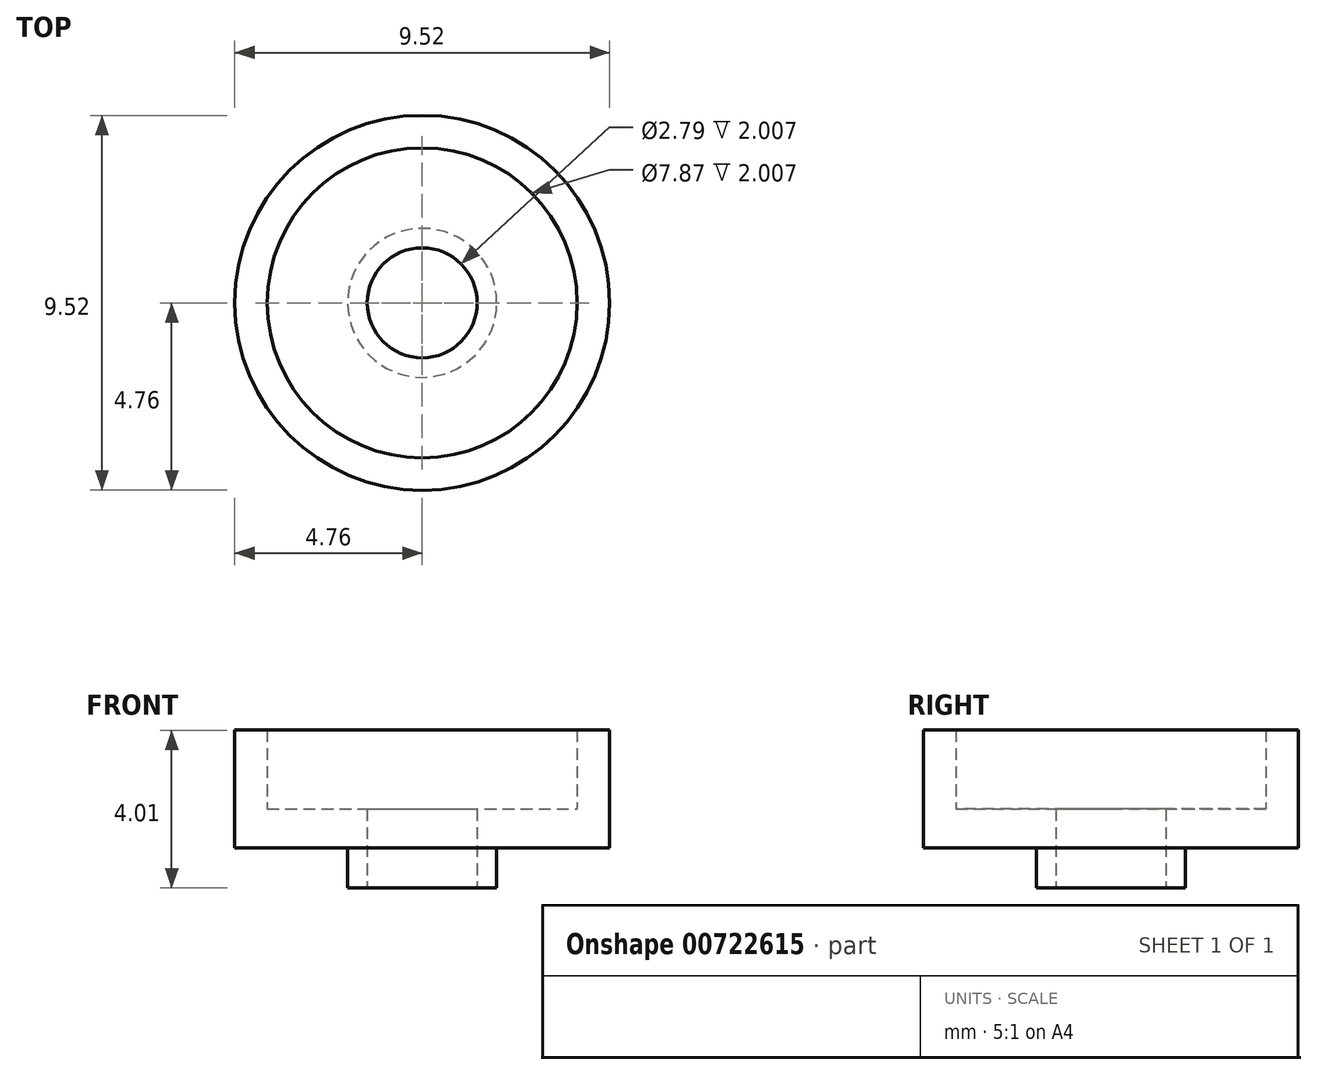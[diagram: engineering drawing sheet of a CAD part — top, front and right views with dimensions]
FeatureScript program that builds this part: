
annotation { "Feature Type Name" : "Feature", "Feature Type Description" : "" }
export const myFeature = defineFeature(function(context is Context, id is Id, definition is map)
    precondition{}
    {
        {
            var Q0;
            Q0=qCreatedBy(makeId("Front.planeOp"),FACE);
            var sketch = newSketch(context, id + "F0", { "sketchPlane" : qUnion([Q0])});
            skLineSegment(sketch, "E0", {"start": v(0, 0) * mm, "end": v(-1.9, 0) * mm});
            skLineSegment(sketch, "E1", {"start": v(-1.9, 0) * mm, "end": v(-1.9, 1.02) * mm});
            skLineSegment(sketch, "E2", {"start": v(-1.9, 1.02) * mm, "end": v(-4.76, 1.02) * mm});
            skLineSegment(sketch, "E3", {"start": v(-4.76, 1.02) * mm, "end": v(-4.76, 4.01) * mm});
            skLineSegment(sketch, "E4", {"start": v(-4.76, 4.01) * mm, "end": v(-3.94, 4.01) * mm});
            skLineSegment(sketch, "E5", {"start": v(-3.94, 4.01) * mm, "end": v(-3.94, 2) * mm});
            skLineSegment(sketch, "E6", {"start": v(-3.94, 2) * mm, "end": v(-1.4, 2) * mm});
            skLineSegment(sketch, "E7", {"start": v(-1.4, 2) * mm, "end": v(-1.4, 0) * mm});
            skLineSegment(sketch, "E8", {"start": v(-1.4, 0) * mm, "end": v(0, 0) * mm});
            skLineSegment(sketch, "E9", {"start": v(0, 0) * mm, "end": v(0, 2) * mm, "construction": true});
            skSolve(sketch);
        }
        {
            var Q0;
            Q0 = qSketchRegion(id + "F0", true);
            var Q1;
            Q1=sQuery(id+"F0.wireOp",EDGE,"E9");
            revolve(context, id + "F1", {"surfaceOperationType" : NewSurfaceOperationType.NEW, "entities" : qUnion([Q0]), "axis" : qUnion([Q1]), "revolveType" : RevolveType.FULL});
        }
    });
